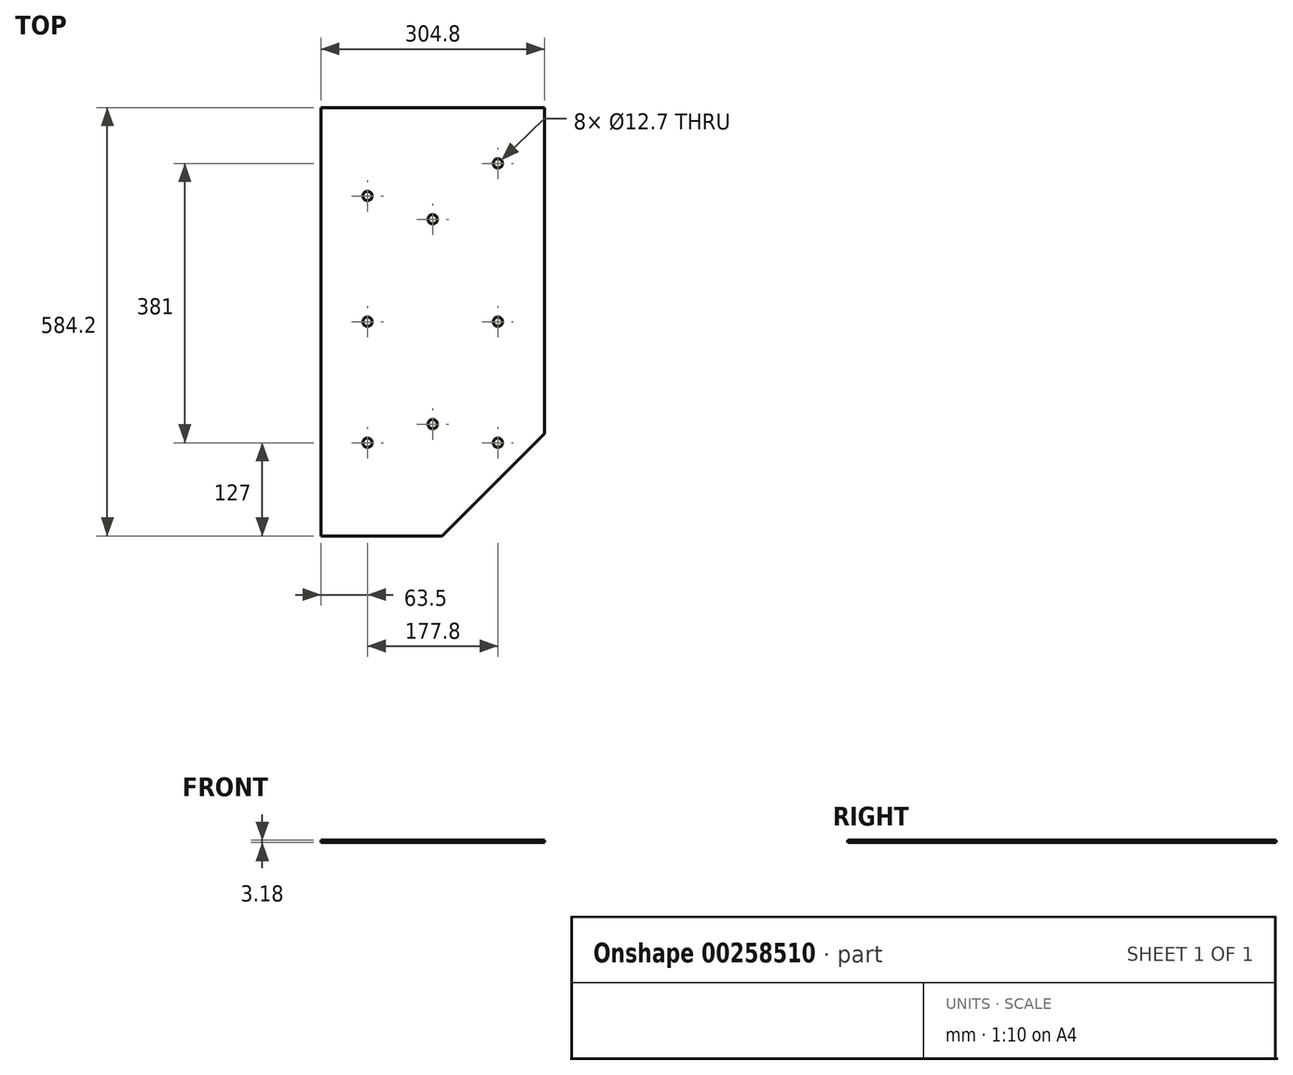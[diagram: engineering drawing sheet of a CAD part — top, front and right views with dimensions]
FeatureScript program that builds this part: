
annotation { "Feature Type Name" : "Feature", "Feature Type Description" : "" }
export const myFeature = defineFeature(function(context is Context, id is Id, definition is map)
    precondition{}
    {
        {
            var Q0;
            Q0=qCreatedBy(makeId("Top.planeOp"),FACE);
            var sketch = newSketch(context, id + "F0", { "sketchPlane" : qUnion([Q0])});
            skLineSegment(sketch, "E0.bottom", {"start": v(152.4, 292.1) * mm, "end": v(-152.4, 292.1) * mm});
            skLineSegment(sketch, "E0.top", {"start": v(12.7, -292.1) * mm, "end": v(-152.4, -292.1) * mm});
            skLineSegment(sketch, "E0.left", {"start": v(152.4, 292.1) * mm, "end": v(152.4, -152.4) * mm});
            skLineSegment(sketch, "E0.right", {"start": v(-152.4, 292.1) * mm, "end": v(-152.4, -292.1) * mm});
            skPoint(sketch, "E0.middle", {"position": v(0, 0) * mm});
            skLineSegment(sketch, "E1", {"start": v(12.7, -292.1) * mm, "end": v(152.4, -152.4) * mm});
            skPoint(sketch, "E2.orphan", {"position": v(152.4, -292.1) * mm});
            skLineSegment(sketch, "E3", {"start": v(-88.9, 292.1) * mm, "end": v(-88.9, 165.1) * mm});
            skLineSegment(sketch, "E4", {"start": v(88.9, 292.1) * mm, "end": v(88.9, 209.55) * mm});
            skLineSegment(sketch, "E5", {"start": v(-95.25, -165.1) * mm, "end": v(-82.55, -165.1) * mm});
            skCircle(sketch, "E6", {"center": v(-88.9, 0) * mm, "radius": 6.35 * mm});
            skCircle(sketch, "E7", {"center": v(88.9, 0) * mm, "radius": 6.35 * mm});
            skCircle(sketch, "E8", {"center": v(-88.9, 171.45) * mm, "radius": 6.35 * mm});
            skCircle(sketch, "E9", {"center": v(88.9, 215.9) * mm, "radius": 6.35 * mm});
            skCircle(sketch, "E10", {"center": v(-88.9, -165.1) * mm, "radius": 6.35 * mm});
            skCircle(sketch, "E11", {"center": v(88.9, -165.1) * mm, "radius": 6.35 * mm});
            skLineSegment(sketch, "E12.trimOffspring", {"start": v(-88.9, 6.35) * mm, "end": v(-88.9, -6.35) * mm});
            skLineSegment(sketch, "E13.trimOffspring", {"start": v(88.9, 6.35) * mm, "end": v(88.9, -6.35) * mm});
            skLineSegment(sketch, "E14.trimOffspring", {"start": v(-88.9, -158.75) * mm, "end": v(-88.9, -292.1) * mm});
            skLineSegment(sketch, "E15.trimOffspring", {"start": v(88.9, -158.75) * mm, "end": v(88.9, -215.9) * mm});
            skLineSegment(sketch, "E16.trimOffspring", {"start": v(82.55, -165.1) * mm, "end": v(139.7, -165.1) * mm});
            skCircle(sketch, "E17", {"center": v(0, 139.7) * mm, "radius": 6.35 * mm});
            skCircle(sketch, "E18", {"center": v(0, -139.7) * mm, "radius": 6.35 * mm});
            skLineSegment(sketch, "E19", {"start": v(0, 0) * mm, "end": v(0, 292.1) * mm, "construction": true});
            skLineSegment(sketch, "E20", {"start": v(0, 292.1) * mm, "end": v(0, -292.1) * mm, "construction": true});
            skLineSegment(sketch, "E21", {"start": v(-88.9, -165.1) * mm, "end": v(139.7, -165.1) * mm, "construction": true});
            skLineSegment(sketch, "E22", {"start": v(-88.9, -165.1) * mm, "end": v(-152.4, -165.1) * mm, "construction": true});
            skSolve(sketch);
        }
        {
            var Q0;
            Q0 = qSketchRegion(id + "F0", true);
            extrude(context, id + "F1", {"entities" : qUnion([Q0]), "depth" : 3.17 * mm});
        }
    });
